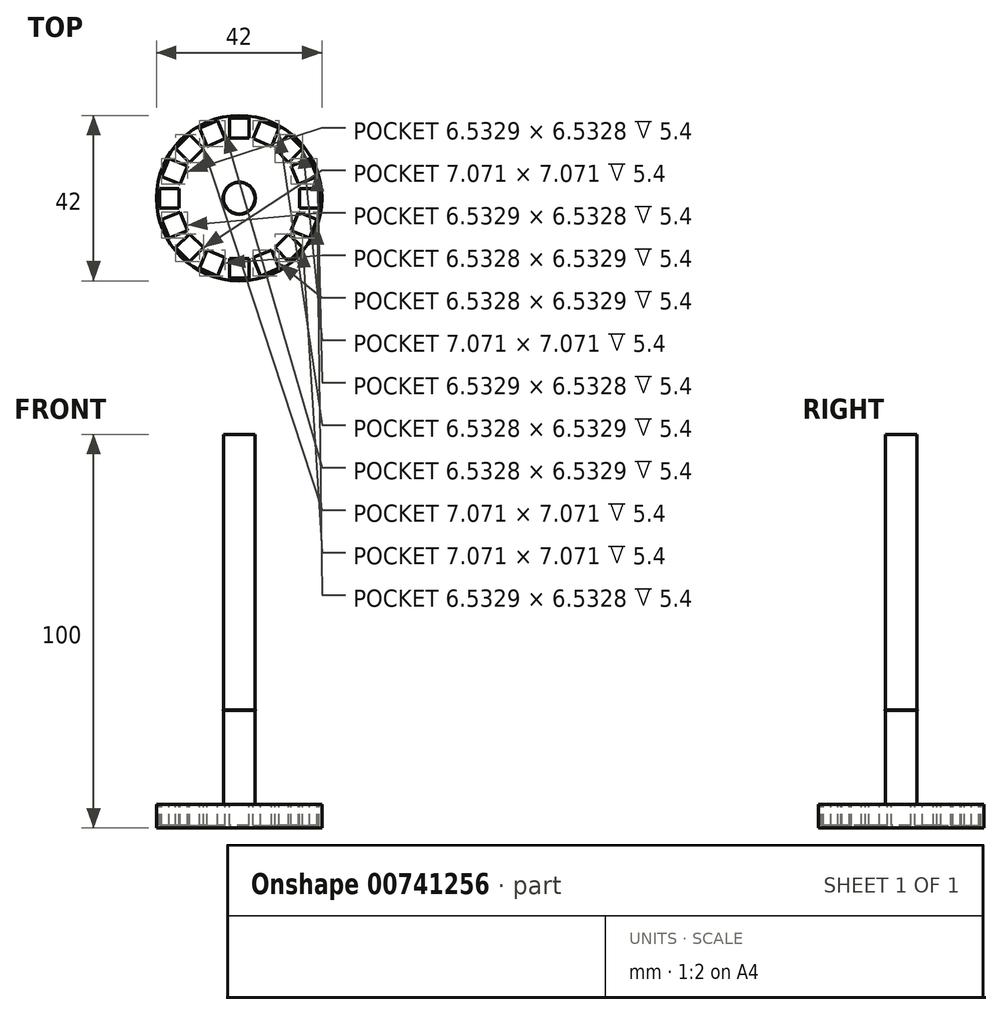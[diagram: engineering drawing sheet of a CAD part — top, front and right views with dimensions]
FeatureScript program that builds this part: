
annotation { "Feature Type Name" : "Feature", "Feature Type Description" : "" }
export const myFeature = defineFeature(function(context is Context, id is Id, definition is map)
    precondition{}
    {
        {
            var Q0;
            Q0=qCreatedBy(makeId("Front.planeOp"),FACE);
            var sketch = newSketch(context, id + "F0", { "sketchPlane" : qUnion([Q0])});
            skLineSegment(sketch, "E0", {"start": v(0, 0) * mm, "end": v(21, 0) * mm});
            skLineSegment(sketch, "E1", {"start": v(21, 0) * mm, "end": v(21, 6) * mm});
            skLineSegment(sketch, "E2", {"start": v(21, 6) * mm, "end": v(0, 6) * mm});
            skLineSegment(sketch, "E3", {"start": v(0, 6) * mm, "end": v(0, 0) * mm});
            skSolve(sketch);
        }
        {
            var Q0;
            Q0=qSketchRegion(id+"F0",true);
            var Q1;
            Q1=sQuery(id+"F0.wireOp",EDGE,"E3");
            revolve(context, id + "F1", {"surfaceOperationType" : NewSurfaceOperationType.NEW, "entities" : qUnion([Q0]), "axis" : qUnion([Q1]), "revolveType" : RevolveType.FULL});
        }
        {
            var Q0;
            Q0=qCreatedBy(makeId("Top.planeOp"),FACE);
            var sketch = newSketch(context, id + "F2", { "sketchPlane" : qUnion([Q0])});
            skCircle(sketch, "E4", {"center": v(0, 0) * mm, "radius": 11 * mm});
            skCircle(sketch, "E5", {"center": v(0, 0) * mm, "radius": 16 * mm});
            skCircle(sketch, "E6", {"center": v(0, 0) * mm, "radius": 21 * mm});
            skCircle(sketch, "E7", {"center": v(0, 0) * mm, "radius": 4 * mm});
            skSolve(sketch);
        }
        {
            var Q0;
            Q0=makeQuery(id+"F2.imprint","IMPRINT",FACE,{"disambiguationData":[TD([[makeQuery(id+"F2.imprint","IMPRINT",EDGE,{"derivedFrom":sQuery(id+"F2.wireOp",EDGE,"E7")}),1.0]])]});
            extrude(context, id + "F3", {"entities" : qUnion([Q0]), "operationType" : NewBodyOperationType.ADD, "depth" : 100 * mm, "offsetDistance" : 25 * mm});
        }
        {
            var Q0;
            Q0=makeQuery(id+"F1.opRevolve","SWEPT_FACE",FACE,{"disambiguationData":[OSD([sQuery(id+"F0.wireOp",EDGE,"E2")])]});
            var sketch = newSketch(context, id + "F4", { "sketchPlane" : qUnion([Q0])});
            skLineSegment(sketch, "E8.bottom", {"start": v(2.5, 15.3) * mm, "end": v(-2.5, 15.3) * mm});
            skLineSegment(sketch, "E8.top", {"start": v(2.5, 20.3) * mm, "end": v(-2.5, 20.3) * mm});
            skLineSegment(sketch, "E8.left", {"start": v(2.5, 15.3) * mm, "end": v(2.5, 20.3) * mm});
            skLineSegment(sketch, "E8.right", {"start": v(-2.5, 15.3) * mm, "end": v(-2.5, 20.3) * mm});
            skLineSegment(sketch, "E9", {"start": v(0, 0) * mm, "end": v(0, 15.3) * mm, "construction": true});
            skLineSegment(sketch, "E10.1.0", {"start": v(-3.55, 15.1) * mm, "end": v(-5.46, 19.71) * mm});
            skLineSegment(sketch, "E10.1.1", {"start": v(-5.46, 19.71) * mm, "end": v(-10.08, 17.8) * mm});
            skLineSegment(sketch, "E10.1.2", {"start": v(-8.16, 13.18) * mm, "end": v(-10.08, 17.8) * mm});
            skLineSegment(sketch, "E10.1.3", {"start": v(-3.55, 15.1) * mm, "end": v(-8.16, 13.18) * mm});
            skLineSegment(sketch, "E10.2.0", {"start": v(-9.05, 12.59) * mm, "end": v(-12.59, 16.12) * mm});
            skLineSegment(sketch, "E10.2.1", {"start": v(-12.59, 16.12) * mm, "end": v(-16.12, 12.59) * mm});
            skLineSegment(sketch, "E10.2.2", {"start": v(-12.59, 9.05) * mm, "end": v(-16.12, 12.59) * mm});
            skLineSegment(sketch, "E10.2.3", {"start": v(-9.05, 12.59) * mm, "end": v(-12.59, 9.05) * mm});
            skLineSegment(sketch, "E10.3.0", {"start": v(-13.18, 8.16) * mm, "end": v(-17.8, 10.08) * mm});
            skLineSegment(sketch, "E10.3.1", {"start": v(-17.8, 10.08) * mm, "end": v(-19.71, 5.46) * mm});
            skLineSegment(sketch, "E10.3.2", {"start": v(-15.1, 3.55) * mm, "end": v(-19.71, 5.46) * mm});
            skLineSegment(sketch, "E10.3.3", {"start": v(-13.18, 8.16) * mm, "end": v(-15.1, 3.55) * mm});
            skLineSegment(sketch, "E10.4.0", {"start": v(-15.3, 2.5) * mm, "end": v(-20.3, 2.5) * mm});
            skLineSegment(sketch, "E10.4.1", {"start": v(-20.3, 2.5) * mm, "end": v(-20.3, -2.5) * mm});
            skLineSegment(sketch, "E10.4.2", {"start": v(-15.3, -2.5) * mm, "end": v(-20.3, -2.5) * mm});
            skLineSegment(sketch, "E10.4.3", {"start": v(-15.3, 2.5) * mm, "end": v(-15.3, -2.5) * mm});
            skLineSegment(sketch, "E10.5.0", {"start": v(-15.1, -3.55) * mm, "end": v(-19.71, -5.46) * mm});
            skLineSegment(sketch, "E10.5.1", {"start": v(-19.71, -5.46) * mm, "end": v(-17.8, -10.08) * mm});
            skLineSegment(sketch, "E10.5.2", {"start": v(-13.18, -8.16) * mm, "end": v(-17.8, -10.08) * mm});
            skLineSegment(sketch, "E10.5.3", {"start": v(-15.1, -3.55) * mm, "end": v(-13.18, -8.16) * mm});
            skLineSegment(sketch, "E10.6.0", {"start": v(-12.59, -9.05) * mm, "end": v(-16.12, -12.59) * mm});
            skLineSegment(sketch, "E10.6.1", {"start": v(-16.12, -12.59) * mm, "end": v(-12.59, -16.12) * mm});
            skLineSegment(sketch, "E10.6.2", {"start": v(-9.05, -12.59) * mm, "end": v(-12.59, -16.12) * mm});
            skLineSegment(sketch, "E10.6.3", {"start": v(-12.59, -9.05) * mm, "end": v(-9.05, -12.59) * mm});
            skLineSegment(sketch, "E10.7.0", {"start": v(-8.16, -13.18) * mm, "end": v(-10.08, -17.8) * mm});
            skLineSegment(sketch, "E10.7.1", {"start": v(-10.08, -17.8) * mm, "end": v(-5.46, -19.71) * mm});
            skLineSegment(sketch, "E10.7.2", {"start": v(-3.55, -15.1) * mm, "end": v(-5.46, -19.71) * mm});
            skLineSegment(sketch, "E10.7.3", {"start": v(-8.16, -13.18) * mm, "end": v(-3.55, -15.1) * mm});
            skLineSegment(sketch, "E10.8.0", {"start": v(-2.5, -15.3) * mm, "end": v(-2.5, -20.3) * mm});
            skLineSegment(sketch, "E10.8.1", {"start": v(-2.5, -20.3) * mm, "end": v(2.5, -20.3) * mm});
            skLineSegment(sketch, "E10.8.2", {"start": v(2.5, -15.3) * mm, "end": v(2.5, -20.3) * mm});
            skLineSegment(sketch, "E10.8.3", {"start": v(-2.5, -15.3) * mm, "end": v(2.5, -15.3) * mm});
            skLineSegment(sketch, "E10.9.0", {"start": v(3.55, -15.1) * mm, "end": v(5.46, -19.71) * mm});
            skLineSegment(sketch, "E10.9.1", {"start": v(5.46, -19.71) * mm, "end": v(10.08, -17.8) * mm});
            skLineSegment(sketch, "E10.9.2", {"start": v(8.16, -13.18) * mm, "end": v(10.08, -17.8) * mm});
            skLineSegment(sketch, "E10.9.3", {"start": v(3.55, -15.1) * mm, "end": v(8.16, -13.18) * mm});
            skLineSegment(sketch, "E10.10.0", {"start": v(9.05, -12.59) * mm, "end": v(12.59, -16.12) * mm});
            skLineSegment(sketch, "E10.10.1", {"start": v(12.59, -16.12) * mm, "end": v(16.12, -12.59) * mm});
            skLineSegment(sketch, "E10.10.2", {"start": v(12.59, -9.05) * mm, "end": v(16.12, -12.59) * mm});
            skLineSegment(sketch, "E10.10.3", {"start": v(9.05, -12.59) * mm, "end": v(12.59, -9.05) * mm});
            skLineSegment(sketch, "E10.11.0", {"start": v(13.18, -8.16) * mm, "end": v(17.8, -10.08) * mm});
            skLineSegment(sketch, "E10.11.1", {"start": v(17.8, -10.08) * mm, "end": v(19.71, -5.46) * mm});
            skLineSegment(sketch, "E10.11.2", {"start": v(15.1, -3.55) * mm, "end": v(19.71, -5.46) * mm});
            skLineSegment(sketch, "E10.11.3", {"start": v(13.18, -8.16) * mm, "end": v(15.1, -3.55) * mm});
            skLineSegment(sketch, "E10.12.0", {"start": v(15.3, -2.5) * mm, "end": v(20.3, -2.5) * mm});
            skLineSegment(sketch, "E10.12.1", {"start": v(20.3, -2.5) * mm, "end": v(20.3, 2.5) * mm});
            skLineSegment(sketch, "E10.12.2", {"start": v(15.3, 2.5) * mm, "end": v(20.3, 2.5) * mm});
            skLineSegment(sketch, "E10.12.3", {"start": v(15.3, -2.5) * mm, "end": v(15.3, 2.5) * mm});
            skLineSegment(sketch, "E10.13.0", {"start": v(15.1, 3.55) * mm, "end": v(19.71, 5.46) * mm});
            skLineSegment(sketch, "E10.13.1", {"start": v(19.71, 5.46) * mm, "end": v(17.8, 10.08) * mm});
            skLineSegment(sketch, "E10.13.2", {"start": v(13.18, 8.16) * mm, "end": v(17.8, 10.08) * mm});
            skLineSegment(sketch, "E10.13.3", {"start": v(15.1, 3.55) * mm, "end": v(13.18, 8.16) * mm});
            skLineSegment(sketch, "E10.14.0", {"start": v(12.59, 9.05) * mm, "end": v(16.12, 12.59) * mm});
            skLineSegment(sketch, "E10.14.1", {"start": v(16.12, 12.59) * mm, "end": v(12.59, 16.12) * mm});
            skLineSegment(sketch, "E10.14.2", {"start": v(9.05, 12.59) * mm, "end": v(12.59, 16.12) * mm});
            skLineSegment(sketch, "E10.14.3", {"start": v(12.59, 9.05) * mm, "end": v(9.05, 12.59) * mm});
            skLineSegment(sketch, "E10.15.0", {"start": v(8.16, 13.18) * mm, "end": v(10.08, 17.8) * mm});
            skLineSegment(sketch, "E10.15.1", {"start": v(10.08, 17.8) * mm, "end": v(5.46, 19.71) * mm});
            skLineSegment(sketch, "E10.15.2", {"start": v(3.55, 15.1) * mm, "end": v(5.46, 19.71) * mm});
            skLineSegment(sketch, "E10.15.3", {"start": v(8.16, 13.18) * mm, "end": v(3.55, 15.1) * mm});
            skPoint(sketch, "E10.center", {"position": v(0, 0) * mm});
            skSolve(sketch);
        }
        {
            var Q0;
            {var subQ0=sQuery(id+"F4.wireOp",EDGE,"6b0e4d02-cffa-4799-8ca5-8f1609af44a9.1.3");Q0=makeQuery(id+"F4.imprint","IMPRINT",FACE,{"disambiguationData":[TD([[makeQuery(id+"F4.imprint","IMPRINT",EDGE,{"derivedFrom":subQ0}),-1.0]])]});}
            var Q1;
            {var subQ0=sQuery(id+"F4.wireOp",EDGE,"E8.bottom");Q1=makeQuery(id+"F4.imprint","IMPRINT",FACE,{"disambiguationData":[TD([[makeQuery(id+"F4.imprint","IMPRINT",EDGE,{"derivedFrom":subQ0}),-1.0]])]});}
            var Q2;
            {var subQ0=sQuery(id+"F4.wireOp",EDGE,"90cd43ab-74c5-4661-9c80-5ee8405ae9ff.9.15.0");Q2=makeQuery(id+"F4.imprint","IMPRINT",FACE,{"disambiguationData":[TD([[makeQuery(id+"F4.imprint","IMPRINT",EDGE,{"derivedFrom":subQ0}),-1.0]])]});}
            var Q3;
            {var subQ0=sQuery(id+"F4.wireOp",EDGE,"90cd43ab-74c5-4661-9c80-5ee8405ae9ff.9.14.0");Q3=makeQuery(id+"F4.imprint","IMPRINT",FACE,{"disambiguationData":[TD([[makeQuery(id+"F4.imprint","IMPRINT",EDGE,{"derivedFrom":subQ0}),-1.0]])]});}
            var Q4;
            {var subQ0=sQuery(id+"F4.wireOp",EDGE,"90cd43ab-74c5-4661-9c80-5ee8405ae9ff.9.13.0");Q4=makeQuery(id+"F4.imprint","IMPRINT",FACE,{"disambiguationData":[TD([[makeQuery(id+"F4.imprint","IMPRINT",EDGE,{"derivedFrom":subQ0}),-1.0]])]});}
            var Q5;
            {var subQ0=sQuery(id+"F4.wireOp",EDGE,"90cd43ab-74c5-4661-9c80-5ee8405ae9ff.9.12.0");Q5=makeQuery(id+"F4.imprint","IMPRINT",FACE,{"disambiguationData":[TD([[makeQuery(id+"F4.imprint","IMPRINT",EDGE,{"derivedFrom":subQ0}),-1.0]])]});}
            var Q6;
            {var subQ0=sQuery(id+"F4.wireOp",EDGE,"90cd43ab-74c5-4661-9c80-5ee8405ae9ff.9.11.0");Q6=makeQuery(id+"F4.imprint","IMPRINT",FACE,{"disambiguationData":[TD([[makeQuery(id+"F4.imprint","IMPRINT",EDGE,{"derivedFrom":subQ0}),-1.0]])]});}
            var Q7;
            {var subQ0=sQuery(id+"F4.wireOp",EDGE,"90cd43ab-74c5-4661-9c80-5ee8405ae9ff.9.10.0");Q7=makeQuery(id+"F4.imprint","IMPRINT",FACE,{"disambiguationData":[TD([[makeQuery(id+"F4.imprint","IMPRINT",EDGE,{"derivedFrom":subQ0}),-1.0]])]});}
            var Q8;
            {var subQ0=sQuery(id+"F4.wireOp",EDGE,"90cd43ab-74c5-4661-9c80-5ee8405ae9ff.9.9.0");Q8=makeQuery(id+"F4.imprint","IMPRINT",FACE,{"disambiguationData":[TD([[makeQuery(id+"F4.imprint","IMPRINT",EDGE,{"derivedFrom":subQ0}),-1.0]])]});}
            var Q9;
            {var subQ0=sQuery(id+"F4.wireOp",EDGE,"90cd43ab-74c5-4661-9c80-5ee8405ae9ff.9.8.0");Q9=makeQuery(id+"F4.imprint","IMPRINT",FACE,{"disambiguationData":[TD([[makeQuery(id+"F4.imprint","IMPRINT",EDGE,{"derivedFrom":subQ0}),-1.0]])]});}
            var Q10;
            {var subQ0=sQuery(id+"F4.wireOp",EDGE,"90cd43ab-74c5-4661-9c80-5ee8405ae9ff.9.7.0");Q10=makeQuery(id+"F4.imprint","IMPRINT",FACE,{"disambiguationData":[TD([[makeQuery(id+"F4.imprint","IMPRINT",EDGE,{"derivedFrom":subQ0}),-1.0]])]});}
            var Q11;
            {var subQ0=sQuery(id+"F4.wireOp",EDGE,"90cd43ab-74c5-4661-9c80-5ee8405ae9ff.9.6.0");Q11=makeQuery(id+"F4.imprint","IMPRINT",FACE,{"disambiguationData":[TD([[makeQuery(id+"F4.imprint","IMPRINT",EDGE,{"derivedFrom":subQ0}),-1.0]])]});}
            var Q12;
            {var subQ0=sQuery(id+"F4.wireOp",EDGE,"90cd43ab-74c5-4661-9c80-5ee8405ae9ff.9.5.0");Q12=makeQuery(id+"F4.imprint","IMPRINT",FACE,{"disambiguationData":[TD([[makeQuery(id+"F4.imprint","IMPRINT",EDGE,{"derivedFrom":subQ0}),-1.0]])]});}
            var Q13;
            {var subQ0=sQuery(id+"F4.wireOp",EDGE,"90cd43ab-74c5-4661-9c80-5ee8405ae9ff.9.4.0");Q13=makeQuery(id+"F4.imprint","IMPRINT",FACE,{"disambiguationData":[TD([[makeQuery(id+"F4.imprint","IMPRINT",EDGE,{"derivedFrom":subQ0}),-1.0]])]});}
            var Q14;
            {var subQ0=sQuery(id+"F4.wireOp",EDGE,"90cd43ab-74c5-4661-9c80-5ee8405ae9ff.9.3.0");Q14=makeQuery(id+"F4.imprint","IMPRINT",FACE,{"disambiguationData":[TD([[makeQuery(id+"F4.imprint","IMPRINT",EDGE,{"derivedFrom":subQ0}),-1.0]])]});}
            var Q15;
            {var subQ0=sQuery(id+"F4.wireOp",EDGE,"6b0e4d02-cffa-4799-8ca5-8f1609af44a9.2.3");Q15=makeQuery(id+"F4.imprint","IMPRINT",FACE,{"disambiguationData":[TD([[makeQuery(id+"F4.imprint","IMPRINT",EDGE,{"derivedFrom":subQ0}),-1.0]])]});}
            var Q16;
            Q16=makeQuery(id+"F4.imprint","IMPRINT",FACE,{"disambiguationData":[TD([[makeQuery(id+"F4.imprint","IMPRINT",EDGE,{"derivedFrom":sQuery(id+"F4.wireOp",EDGE,"3ac6aee8-8570-404a-83dd-43d2a112f3a3.1.0")}),-1.0]])]});
            var Q17;
            Q17=makeQuery(id+"F4.imprint","IMPRINT",FACE,{"disambiguationData":[TD([[makeQuery(id+"F4.imprint","IMPRINT",EDGE,{"derivedFrom":sQuery(id+"F4.wireOp",EDGE,"3ac6aee8-8570-404a-83dd-43d2a112f3a3.15.0")}),-1.0]])]});
            var Q18;
            Q18=makeQuery(id+"F4.imprint","IMPRINT",FACE,{"disambiguationData":[TD([[makeQuery(id+"F4.imprint","IMPRINT",EDGE,{"derivedFrom":sQuery(id+"F4.wireOp",EDGE,"3ac6aee8-8570-404a-83dd-43d2a112f3a3.14.0")}),-1.0]])]});
            var Q19;
            Q19=makeQuery(id+"F4.imprint","IMPRINT",FACE,{"disambiguationData":[TD([[makeQuery(id+"F4.imprint","IMPRINT",EDGE,{"derivedFrom":sQuery(id+"F4.wireOp",EDGE,"3ac6aee8-8570-404a-83dd-43d2a112f3a3.13.0")}),-1.0]])]});
            var Q20;
            Q20=makeQuery(id+"F4.imprint","IMPRINT",FACE,{"disambiguationData":[TD([[makeQuery(id+"F4.imprint","IMPRINT",EDGE,{"derivedFrom":sQuery(id+"F4.wireOp",EDGE,"3ac6aee8-8570-404a-83dd-43d2a112f3a3.12.0")}),-1.0]])]});
            var Q21;
            Q21=makeQuery(id+"F4.imprint","IMPRINT",FACE,{"disambiguationData":[TD([[makeQuery(id+"F4.imprint","IMPRINT",EDGE,{"derivedFrom":sQuery(id+"F4.wireOp",EDGE,"3ac6aee8-8570-404a-83dd-43d2a112f3a3.11.0")}),-1.0]])]});
            var Q22;
            Q22=makeQuery(id+"F4.imprint","IMPRINT",FACE,{"disambiguationData":[TD([[makeQuery(id+"F4.imprint","IMPRINT",EDGE,{"derivedFrom":sQuery(id+"F4.wireOp",EDGE,"3ac6aee8-8570-404a-83dd-43d2a112f3a3.10.0")}),-1.0]])]});
            var Q23;
            Q23=makeQuery(id+"F4.imprint","IMPRINT",FACE,{"disambiguationData":[TD([[makeQuery(id+"F4.imprint","IMPRINT",EDGE,{"derivedFrom":sQuery(id+"F4.wireOp",EDGE,"3ac6aee8-8570-404a-83dd-43d2a112f3a3.9.0")}),-1.0]])]});
            var Q24;
            Q24=makeQuery(id+"F4.imprint","IMPRINT",FACE,{"disambiguationData":[TD([[makeQuery(id+"F4.imprint","IMPRINT",EDGE,{"derivedFrom":sQuery(id+"F4.wireOp",EDGE,"3ac6aee8-8570-404a-83dd-43d2a112f3a3.8.0")}),-1.0]])]});
            var Q25;
            Q25=makeQuery(id+"F4.imprint","IMPRINT",FACE,{"disambiguationData":[TD([[makeQuery(id+"F4.imprint","IMPRINT",EDGE,{"derivedFrom":sQuery(id+"F4.wireOp",EDGE,"3ac6aee8-8570-404a-83dd-43d2a112f3a3.7.0")}),-1.0]])]});
            var Q26;
            Q26=makeQuery(id+"F4.imprint","IMPRINT",FACE,{"disambiguationData":[TD([[makeQuery(id+"F4.imprint","IMPRINT",EDGE,{"derivedFrom":sQuery(id+"F4.wireOp",EDGE,"3ac6aee8-8570-404a-83dd-43d2a112f3a3.6.0")}),-1.0]])]});
            var Q27;
            Q27=makeQuery(id+"F4.imprint","IMPRINT",FACE,{"disambiguationData":[TD([[makeQuery(id+"F4.imprint","IMPRINT",EDGE,{"derivedFrom":sQuery(id+"F4.wireOp",EDGE,"3ac6aee8-8570-404a-83dd-43d2a112f3a3.5.0")}),-1.0]])]});
            var Q28;
            Q28=makeQuery(id+"F4.imprint","IMPRINT",FACE,{"disambiguationData":[TD([[makeQuery(id+"F4.imprint","IMPRINT",EDGE,{"derivedFrom":sQuery(id+"F4.wireOp",EDGE,"3ac6aee8-8570-404a-83dd-43d2a112f3a3.4.0")}),-1.0]])]});
            var Q29;
            Q29=makeQuery(id+"F4.imprint","IMPRINT",FACE,{"disambiguationData":[TD([[makeQuery(id+"F4.imprint","IMPRINT",EDGE,{"derivedFrom":sQuery(id+"F4.wireOp",EDGE,"3ac6aee8-8570-404a-83dd-43d2a112f3a3.3.0")}),-1.0]])]});
            var Q30;
            Q30=makeQuery(id+"F4.imprint","IMPRINT",FACE,{"disambiguationData":[TD([[makeQuery(id+"F4.imprint","IMPRINT",EDGE,{"derivedFrom":sQuery(id+"F4.wireOp",EDGE,"3ac6aee8-8570-404a-83dd-43d2a112f3a3.2.0")}),-1.0]])]});
            var Q31;
            Q31=makeQuery(id+"F4.imprint","IMPRINT",FACE,{"disambiguationData":[TD([[makeQuery(id+"F4.imprint","IMPRINT",EDGE,{"derivedFrom":sQuery(id+"F4.wireOp",EDGE,"E10.1.0")}),1.0]])]});
            var Q32;
            Q32=makeQuery(id+"F4.imprint","IMPRINT",FACE,{"disambiguationData":[TD([[makeQuery(id+"F4.imprint","IMPRINT",EDGE,{"derivedFrom":sQuery(id+"F4.wireOp",EDGE,"E10.15.0")}),1.0]])]});
            var Q33;
            Q33=makeQuery(id+"F4.imprint","IMPRINT",FACE,{"disambiguationData":[TD([[makeQuery(id+"F4.imprint","IMPRINT",EDGE,{"derivedFrom":sQuery(id+"F4.wireOp",EDGE,"E10.14.0")}),1.0]])]});
            var Q34;
            Q34=makeQuery(id+"F4.imprint","IMPRINT",FACE,{"disambiguationData":[TD([[makeQuery(id+"F4.imprint","IMPRINT",EDGE,{"derivedFrom":sQuery(id+"F4.wireOp",EDGE,"E10.13.0")}),1.0]])]});
            var Q35;
            Q35=makeQuery(id+"F4.imprint","IMPRINT",FACE,{"disambiguationData":[TD([[makeQuery(id+"F4.imprint","IMPRINT",EDGE,{"derivedFrom":sQuery(id+"F4.wireOp",EDGE,"E10.12.0")}),1.0]])]});
            var Q36;
            Q36=makeQuery(id+"F4.imprint","IMPRINT",FACE,{"disambiguationData":[TD([[makeQuery(id+"F4.imprint","IMPRINT",EDGE,{"derivedFrom":sQuery(id+"F4.wireOp",EDGE,"E10.11.0")}),1.0]])]});
            var Q37;
            Q37=makeQuery(id+"F4.imprint","IMPRINT",FACE,{"disambiguationData":[TD([[makeQuery(id+"F4.imprint","IMPRINT",EDGE,{"derivedFrom":sQuery(id+"F4.wireOp",EDGE,"E10.10.0")}),1.0]])]});
            var Q38;
            Q38=makeQuery(id+"F4.imprint","IMPRINT",FACE,{"disambiguationData":[TD([[makeQuery(id+"F4.imprint","IMPRINT",EDGE,{"derivedFrom":sQuery(id+"F4.wireOp",EDGE,"E10.2.0")}),1.0]])]});
            var Q39;
            Q39=makeQuery(id+"F4.imprint","IMPRINT",FACE,{"disambiguationData":[TD([[makeQuery(id+"F4.imprint","IMPRINT",EDGE,{"derivedFrom":sQuery(id+"F4.wireOp",EDGE,"E10.3.0")}),1.0]])]});
            var Q40;
            Q40=makeQuery(id+"F4.imprint","IMPRINT",FACE,{"disambiguationData":[TD([[makeQuery(id+"F4.imprint","IMPRINT",EDGE,{"derivedFrom":sQuery(id+"F4.wireOp",EDGE,"E10.4.0")}),1.0]])]});
            var Q41;
            Q41=makeQuery(id+"F4.imprint","IMPRINT",FACE,{"disambiguationData":[TD([[makeQuery(id+"F4.imprint","IMPRINT",EDGE,{"derivedFrom":sQuery(id+"F4.wireOp",EDGE,"E10.5.0")}),1.0]])]});
            var Q42;
            Q42=makeQuery(id+"F4.imprint","IMPRINT",FACE,{"disambiguationData":[TD([[makeQuery(id+"F4.imprint","IMPRINT",EDGE,{"derivedFrom":sQuery(id+"F4.wireOp",EDGE,"E10.6.0")}),1.0]])]});
            var Q43;
            Q43=makeQuery(id+"F4.imprint","IMPRINT",FACE,{"disambiguationData":[TD([[makeQuery(id+"F4.imprint","IMPRINT",EDGE,{"derivedFrom":sQuery(id+"F4.wireOp",EDGE,"E10.7.0")}),1.0]])]});
            var Q44;
            Q44=makeQuery(id+"F4.imprint","IMPRINT",FACE,{"disambiguationData":[TD([[makeQuery(id+"F4.imprint","IMPRINT",EDGE,{"derivedFrom":sQuery(id+"F4.wireOp",EDGE,"E10.8.0")}),1.0]])]});
            var Q45;
            Q45=makeQuery(id+"F4.imprint","IMPRINT",FACE,{"disambiguationData":[TD([[makeQuery(id+"F4.imprint","IMPRINT",EDGE,{"derivedFrom":sQuery(id+"F4.wireOp",EDGE,"E10.9.0")}),1.0]])]});
            extrude(context, id + "F5", {"entities" : qUnion([Q0, Q1, Q2, Q3, Q4, Q5, Q6, Q7, Q8, Q9, Q10, Q11, Q12, Q13, Q14, Q15, Q16, Q17, Q18, Q19, Q20, Q21, Q22, Q23, Q24, Q25, Q26, Q27, Q28, Q29, Q30, Q31, Q32, Q33, Q34, Q35, Q36, Q37, Q38, Q39, Q40, Q41, Q42, Q43, Q44, Q45]), "operationType" : NewBodyOperationType.REMOVE, "oppositeDirection" : true, "depth" : 5.4 * mm, "offsetDistance" : 25 * mm});
        }
        {
            var Q0;
            Q0=qCreatedBy(makeId("Right.planeOp"),FACE);
            var sketch = newSketch(context, id + "F6", { "sketchPlane" : qUnion([Q0])});
            skLineSegment(sketch, "E11", {"start": v(0, 0) * mm, "end": v(0, 30) * mm});
            skLineSegment(sketch, "E12", {"start": v(0, 30) * mm, "end": v(4.1, 30) * mm});
            skLineSegment(sketch, "E13", {"start": v(4.1, 30) * mm, "end": v(-5.9, 30) * mm});
            skLineSegment(sketch, "E14.top", {"start": v(0, 29.8) * mm, "end": v(4.1, 29.8) * mm});
            skLineSegment(sketch, "E14.left", {"start": v(0, 30) * mm, "end": v(0, 29.8) * mm});
            skLineSegment(sketch, "E14.right", {"start": v(4.1, 30) * mm, "end": v(4.1, 29.8) * mm});
            skSolve(sketch);
        }
        {
            var Q0;
            Q0 = qSketchRegion(id + "F6", true);
            var Q1;
            Q1=sQuery(id+"F6.wireOp",EDGE,"E14.left");
            revolve(context, id + "F7", {"operationType" : NewBodyOperationType.ADD, "surfaceOperationType" : NewSurfaceOperationType.NEW, "entities" : qUnion([Q0]), "axis" : qUnion([Q1]), "revolveType" : RevolveType.FULL});
        }
    });
